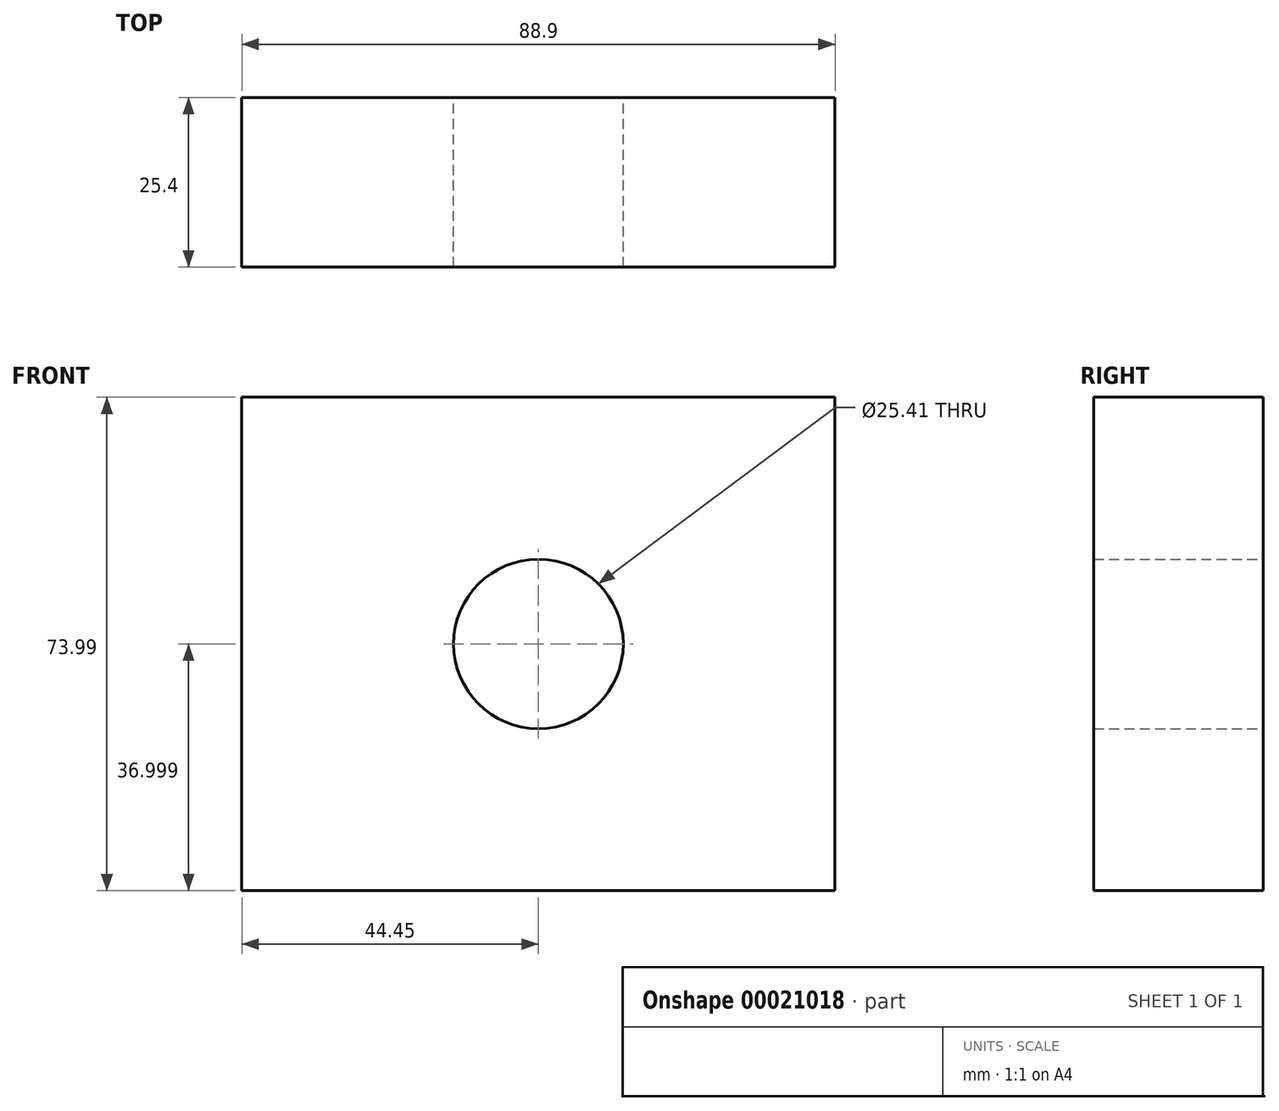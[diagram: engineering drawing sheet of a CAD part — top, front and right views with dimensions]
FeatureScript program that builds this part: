
annotation { "Feature Type Name" : "Feature", "Feature Type Description" : "" }
export const myFeature = defineFeature(function(context is Context, id is Id, definition is map)
    precondition{}
    {
        {
            var Q0;
            Q0=qCreatedBy(makeId("Front.planeOp"),FACE);
            var sketch = newSketch(context, id + "F0", { "sketchPlane" : qUnion([Q0])});
            skLineSegment(sketch, "E0.bottom", {"start": v(-42.64, 30.27) * mm, "end": v(46.26, 30.27) * mm});
            skLineSegment(sketch, "E0.top", {"start": v(-42.64, -43.72) * mm, "end": v(46.26, -43.72) * mm});
            skLineSegment(sketch, "E0.left", {"start": v(-42.64, 30.27) * mm, "end": v(-42.64, -43.72) * mm});
            skLineSegment(sketch, "E0.right", {"start": v(46.26, 30.27) * mm, "end": v(46.26, -43.72) * mm});
            skLineSegment(sketch, "E1", {"start": v(-42.64, -6.72) * mm, "end": v(46.26, -6.72) * mm});
            skLineSegment(sketch, "E2", {"start": v(1.8, 30.27) * mm, "end": v(1.8, -43.72) * mm});
            skCircle(sketch, "E3", {"center": v(1.8, -6.72) * mm, "radius": 12.7 * mm});
            skSolve(sketch);
        }
        {
            var Q0;
            Q0 = qSketchRegion(id + "F0", true);
            extrude(context, id + "F1", {"entities" : qUnion([Q0]), "depth" : 25.4 * mm});
        }
    });
